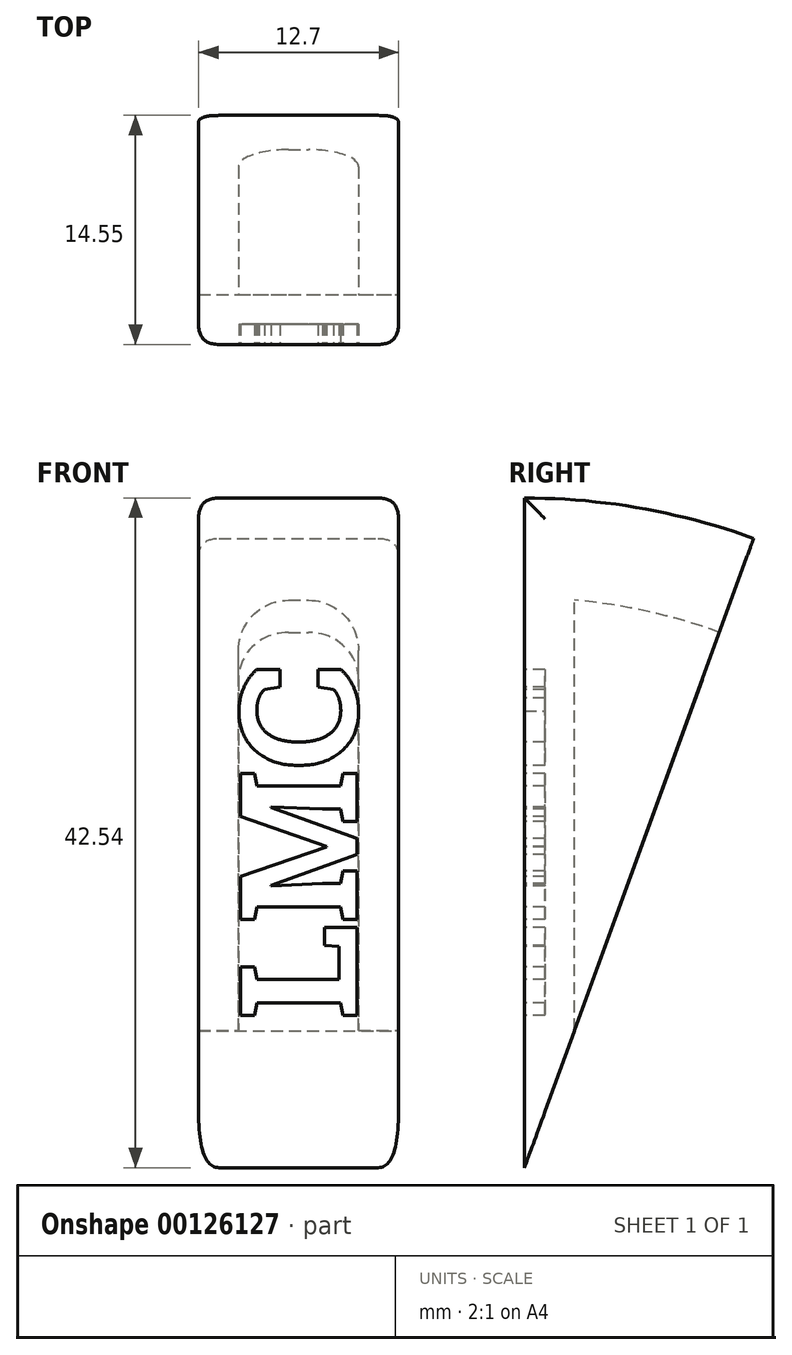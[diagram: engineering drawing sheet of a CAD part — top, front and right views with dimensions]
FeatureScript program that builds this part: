
annotation { "Feature Type Name" : "Feature", "Feature Type Description" : "" }
export const myFeature = defineFeature(function(context is Context, id is Id, definition is map)
    precondition{}
    {
        {
            var Q0;
            Q0=qCreatedBy(makeId("Front.planeOp"),FACE);
            var sketch = newSketch(context, id + "F0", { "sketchPlane" : qUnion([Q0])});
            skLineSegment(sketch, "E0.bottom", {"start": v(-11.66, 42.54) * mm, "end": v(1.04, 42.54) * mm});
            skLineSegment(sketch, "E0.top", {"start": v(-11.66, 0) * mm, "end": v(1.04, 0) * mm});
            skLineSegment(sketch, "E0.left", {"start": v(-11.66, 42.54) * mm, "end": v(-11.66, 0) * mm});
            skLineSegment(sketch, "E0.right", {"start": v(1.04, 42.54) * mm, "end": v(1.04, 0) * mm});
            skLineSegment(sketch, "E1.bottom", {"start": v(-5.95, 36.19) * mm, "end": v(-4.68, 36.19) * mm});
            skLineSegment(sketch, "E1.top", {"start": v(-9.12, 0) * mm, "end": v(-1.5, 0) * mm});
            skLineSegment(sketch, "E1.left", {"start": v(-9.12, 33.01) * mm, "end": v(-9.12, 0) * mm});
            skLineSegment(sketch, "E1.right", {"start": v(-1.5, 33.01) * mm, "end": v(-1.5, 0) * mm});
            skArc(sketch, "E2.filletArc", {"start": v(-5.95, 36.19) * mm, "mid": v(-8.2, 35.26) * mm, "end": v(-9.12, 33.01) * mm});
            skArc(sketch, "E3.filletArc", {"start": v(-1.5, 33.01) * mm, "mid": v(-2.43, 35.26) * mm, "end": v(-4.68, 36.19) * mm});
            skLineSegment(sketch, "E4", {"start": v(-11.66, 39.13) * mm, "end": v(1.04, 39.13) * mm});
            skSolve(sketch);
        }
        {
            var Q0;
            Q0=makeQuery(id+"F0.imprint","IMPRINT",FACE,{"disambiguationData":[TD([[makeQuery(id+"F0.imprint","IMPRINT",EDGE,{"derivedFrom":sQuery(id+"F0.wireOp",EDGE,"E0.bottom")}),-1.0]])]});
            var Q1;
            Q1=makeQuery(id+"F0.imprint","IMPRINT",FACE,{"disambiguationData":[TD([[makeQuery(id+"F0.imprint","IMPRINT",EDGE,{"derivedFrom":sQuery(id+"F0.wireOp",EDGE,"E1.bottom")}),1.0]])]});
            var Q2;
            Q2=sQuery(id+"F0.wireOp",EDGE,"E1.top");
            revolve(context, id + "F1", {"entities" : qUnion([Q0, Q1]), "axis" : qUnion([Q2]), "revolveType" : RevolveType.ONE_DIRECTION, "oppositeDirection" : true, "angle" : 20 * degree});
        }
        {
            var Q0;
            Q0=makeQuery(id+"F0.imprint","IMPRINT",FACE,{"disambiguationData":[TD([[makeQuery(id+"F0.imprint","IMPRINT",EDGE,{"derivedFrom":sQuery(id+"F0.wireOp",EDGE,"E0.bottom")}),-1.0]])]});
            var Q1;
            Q1=makeQuery(id+"F0.imprint","IMPRINT",FACE,{"disambiguationData":[TD([[makeQuery(id+"F0.imprint","IMPRINT",EDGE,{"derivedFrom":sQuery(id+"F0.wireOp",EDGE,"E1.bottom")}),-1.0]])]});
            var Q2;
            Q2=sQuery(id+"F0.wireOp",EDGE,"E1.top");
            revolve(context, id + "F2", {"entities" : qUnion([Q0, Q1]), "axis" : qUnion([Q2]), "revolveType" : RevolveType.ONE_DIRECTION, "oppositeDirection" : true, "angle" : 5 * degree});
        }
        {
            var Q0;
            Q0=makeQuery(id+"F0.imprint","IMPRINT",FACE,{"disambiguationData":[TD([[makeQuery(id+"F0.imprint","IMPRINT",EDGE,{"derivedFrom":sQuery(id+"F0.wireOp",EDGE,"E1.bottom")}),1.0]])]});
            var Q1;
            Q1=makeQuery(id+"F0.imprint","IMPRINT",FACE,{"disambiguationData":[TD([[makeQuery(id+"F0.imprint","IMPRINT",EDGE,{"derivedFrom":sQuery(id+"F0.wireOp",EDGE,"E1.bottom")}),-1.0]])]});
            extrude(context, id + "F3", {"entities" : qUnion([Q0, Q1]), "operationType" : NewBodyOperationType.ADD, "oppositeDirection" : true, "depth" : 3.17 * mm});
        }
        {
            var Q0;
            Q0=qCreatedBy(makeId("Right.planeOp"),FACE);
            var sketch = newSketch(context, id + "F4", { "sketchPlane" : qUnion([Q0])});
            skLineSegment(sketch, "E5", {"start": v(-3.2, 8.75) * mm, "end": v(0, 0) * mm});
            skLineSegment(sketch, "E6", {"start": v(0, 0) * mm, "end": v(-5.99, 0) * mm});
            skLineSegment(sketch, "E7", {"start": v(-5.99, 0) * mm, "end": v(-3.2, 8.75) * mm});
            skLineSegment(sketch, "E8.MirrorCS", {"start": v(3.2, 8.75) * mm, "end": v(0, 0) * mm});
            skLineSegment(sketch, "E9.MirrorCS", {"start": v(0, 0) * mm, "end": v(5.99, 0) * mm});
            skLineSegment(sketch, "E10.MirrorCS", {"start": v(5.99, 0) * mm, "end": v(3.2, 8.75) * mm});
            skSolve(sketch);
        }
        {
            var Q0;
            Q0=makeQuery(id+"F4.imprint","IMPRINT",FACE,{"disambiguationData":[TD([[makeQuery(id+"F4.imprint","IMPRINT",EDGE,{"derivedFrom":sQuery(id+"F4.wireOp",EDGE,"E8.MirrorCS")}),1.0]])]});
            extrude(context, id + "F5", {"entities" : qUnion([Q0]), "operationType" : NewBodyOperationType.REMOVE, "endBound" : BoundingType.THROUGH_ALL, "depth" : 25.4 * mm, "hasSecondDirection" : true, "secondDirectionOppositeDirection" : true, "secondDirectionDepth" : 25.4 * mm});
        }
        {
            var Q0;
            Q0=makeQuery(id+"F1.opRevolve","CAP_EDGE",EDGE,{"disambiguationData":[OSD([sQuery(id+"F0.wireOp",EDGE,"E0.right")])],"isStart":true});
            var Q1;
            Q1=makeQuery(id+"F1.opRevolve","CAP_EDGE",EDGE,{"disambiguationData":[OSD([sQuery(id+"F0.wireOp",EDGE,"E0.left")])],"isStart":true});
            var Q2;
            Q2=makeQuery(id+"F1.opRevolve","SWEPT_EDGE",EDGE,{"disambiguationData":[OSD([sQuery(id+"F0.wireOp",EDGE,"E0.bottom"),sQuery(id+"F0.wireOp",EDGE,"E0.right")])]});
            var Q3;
            Q3=makeQuery(id+"F1.opRevolve","SWEPT_EDGE",EDGE,{"disambiguationData":[OSD([sQuery(id+"F0.wireOp",EDGE,"E0.bottom"),sQuery(id+"F0.wireOp",EDGE,"E0.left")])]});
            var Q4;
            {var subQ0=sQuery(id+"F0.wireOp",EDGE,"E0.bottom");Q4=makeQuery(id+"F3.boolean.opBoolean","MERGE",EDGE,{"derivedFrom":[makeQuery(id+"F1.opRevolve","CAP_EDGE",EDGE,{"disambiguationData":[OSD([subQ0])],"isStart":true}),makeQuery(id+"F2.opRevolve","CAP_EDGE",EDGE,{"disambiguationData":[OSD([subQ0])],"isStart":true}),makeQuery(id+"F3.opExtrude","CAP_EDGE",EDGE,{"disambiguationData":[OSD([subQ0])],"isStart":true})]});}
            fillet(context, id + "F6", {"entities" : qUnion([Q0, Q1, Q2, Q3, Q4]), "radius" : 1.3 * mm, "tangentPropagation" : true, "rho" : 0.5, "crossSection" : FilletCrossSection.CONIC, "allowEdgeOverflow" : false});
        }
        {
            var Q0;
            Q0=makeQuery(id+"F0.imprint","IMPRINT",FACE,{"disambiguationData":[TD([[makeQuery(id+"F0.imprint","IMPRINT",EDGE,{"derivedFrom":sQuery(id+"F0.wireOp",EDGE,"E0.bottom")}),-1.0]])]});
            var sketch = newSketch(context, id + "F7", { "sketchPlane" : qUnion([Q0])});
            skText(sketch, "E11", { "text": "LMC", "fontName": "RobotoSlab-Bold.ttf"});
            const initialGuessF7  = {"E11": [-0.0016, 0.0094, 0, 1, 0.00749]};
            skSetInitialGuess(sketch, initialGuessF7);
            skSolve(sketch);
        }
        {
            var Q0;
            Q0 = qSketchRegion(id + "F7", true);
            extrude(context, id + "F8", {"entities" : qUnion([Q0]), "operationType" : NewBodyOperationType.REMOVE, "oppositeDirection" : true, "depth" : 1.3 * mm});
        }
    });
